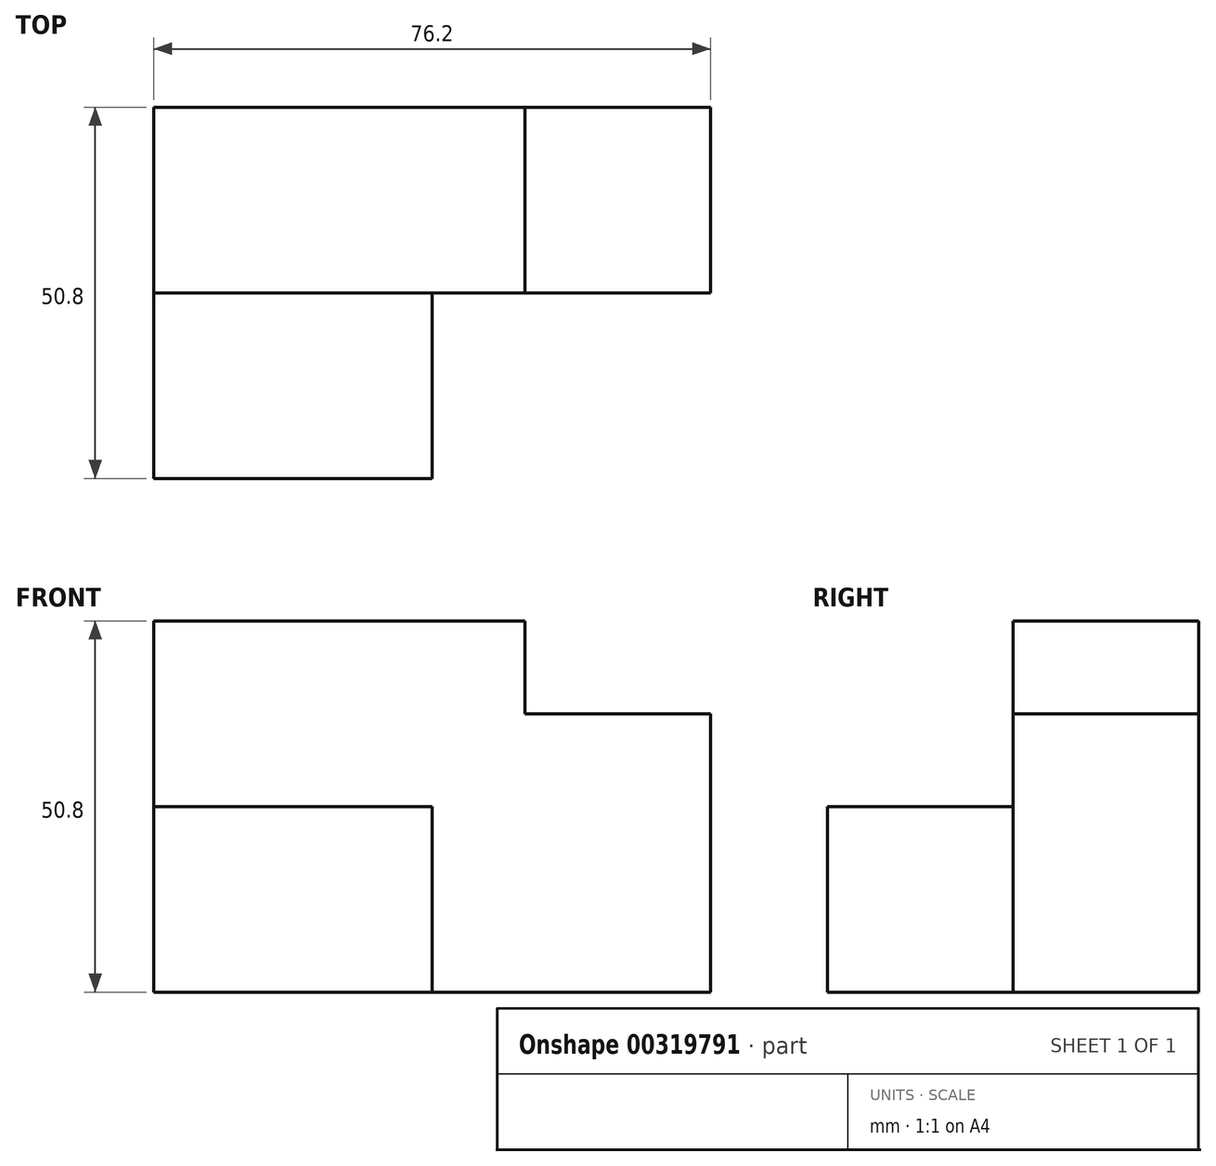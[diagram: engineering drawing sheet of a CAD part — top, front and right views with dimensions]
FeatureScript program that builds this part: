
annotation { "Feature Type Name" : "Feature", "Feature Type Description" : "" }
export const myFeature = defineFeature(function(context is Context, id is Id, definition is map)
    precondition{}
    {
        {
            var Q0;
            Q0=qCreatedBy(makeId("Front.planeOp"),FACE);
            var sketch = newSketch(context, id + "F0", { "sketchPlane" : qUnion([Q0])});
            skLineSegment(sketch, "E0", {"start": v(-52.74, 14.03) * mm, "end": v(-52.74, -36.77) * mm});
            skLineSegment(sketch, "E1", {"start": v(-52.74, -36.77) * mm, "end": v(23.46, -36.77) * mm});
            skLineSegment(sketch, "E2", {"start": v(23.46, -36.77) * mm, "end": v(23.46, 1.33) * mm});
            skLineSegment(sketch, "E3", {"start": v(23.46, 1.33) * mm, "end": v(-1.94, 1.33) * mm});
            skLineSegment(sketch, "E4", {"start": v(-1.94, 1.33) * mm, "end": v(-1.94, 14.03) * mm});
            skLineSegment(sketch, "E5", {"start": v(-1.94, 14.03) * mm, "end": v(-52.74, 14.03) * mm});
            skSolve(sketch);
        }
        {
            var Q0;
            Q0=makeQuery(id+"F0.imprint","IMPRINT",FACE,{"disambiguationData":[TD([[makeQuery(id+"F0.imprint","IMPRINT",EDGE,{"derivedFrom":sQuery(id+"F0.wireOp",EDGE,"E0")}),1.0]])]});
            extrude(context, id + "F1", {"entities" : qUnion([Q0]), "depth" : 25.4 * mm});
        }
        {
            var Q0;
            Q0=makeQuery(id+"F1.opExtrude","CAP_FACE",FACE,{"disambiguationData":[OSD([sQuery(id+"F0.wireOp",EDGE,"E0"),sQuery(id+"F0.wireOp",EDGE,"E1"),sQuery(id+"F0.wireOp",EDGE,"E2"),sQuery(id+"F0.wireOp",EDGE,"E3"),sQuery(id+"F0.wireOp",EDGE,"E4"),sQuery(id+"F0.wireOp",EDGE,"E5")])],"isStart":false});
            var sketch = newSketch(context, id + "F2", { "sketchPlane" : qUnion([Q0])});
            skPoint(sketch, "E6.oppositeSnap0", {"position": v(-14.64, -36.77) * mm});
            skLineSegment(sketch, "E6.bottom", {"start": v(-52.74, -36.77) * mm, "end": v(-14.64, -36.77) * mm});
            skLineSegment(sketch, "E6.top", {"start": v(-52.74, -11.37) * mm, "end": v(-14.64, -11.37) * mm});
            skLineSegment(sketch, "E6.left", {"start": v(-52.74, -36.77) * mm, "end": v(-52.74, -11.37) * mm});
            skLineSegment(sketch, "E6.right", {"start": v(-14.64, -36.77) * mm, "end": v(-14.64, -11.37) * mm});
            skSolve(sketch);
        }
        {
            var Q0;
            Q0=makeQuery(id+"F2.imprint","IMPRINT",FACE,{"disambiguationData":[TD([[makeQuery(id+"F2.imprint","IMPRINT",EDGE,{"derivedFrom":sQuery(id+"F2.wireOp",EDGE,"E6.bottom")}),1.0]])]});
            extrude(context, id + "F3", {"entities" : qUnion([Q0]), "operationType" : NewBodyOperationType.ADD, "depth" : 25.4 * mm});
        }
    });
